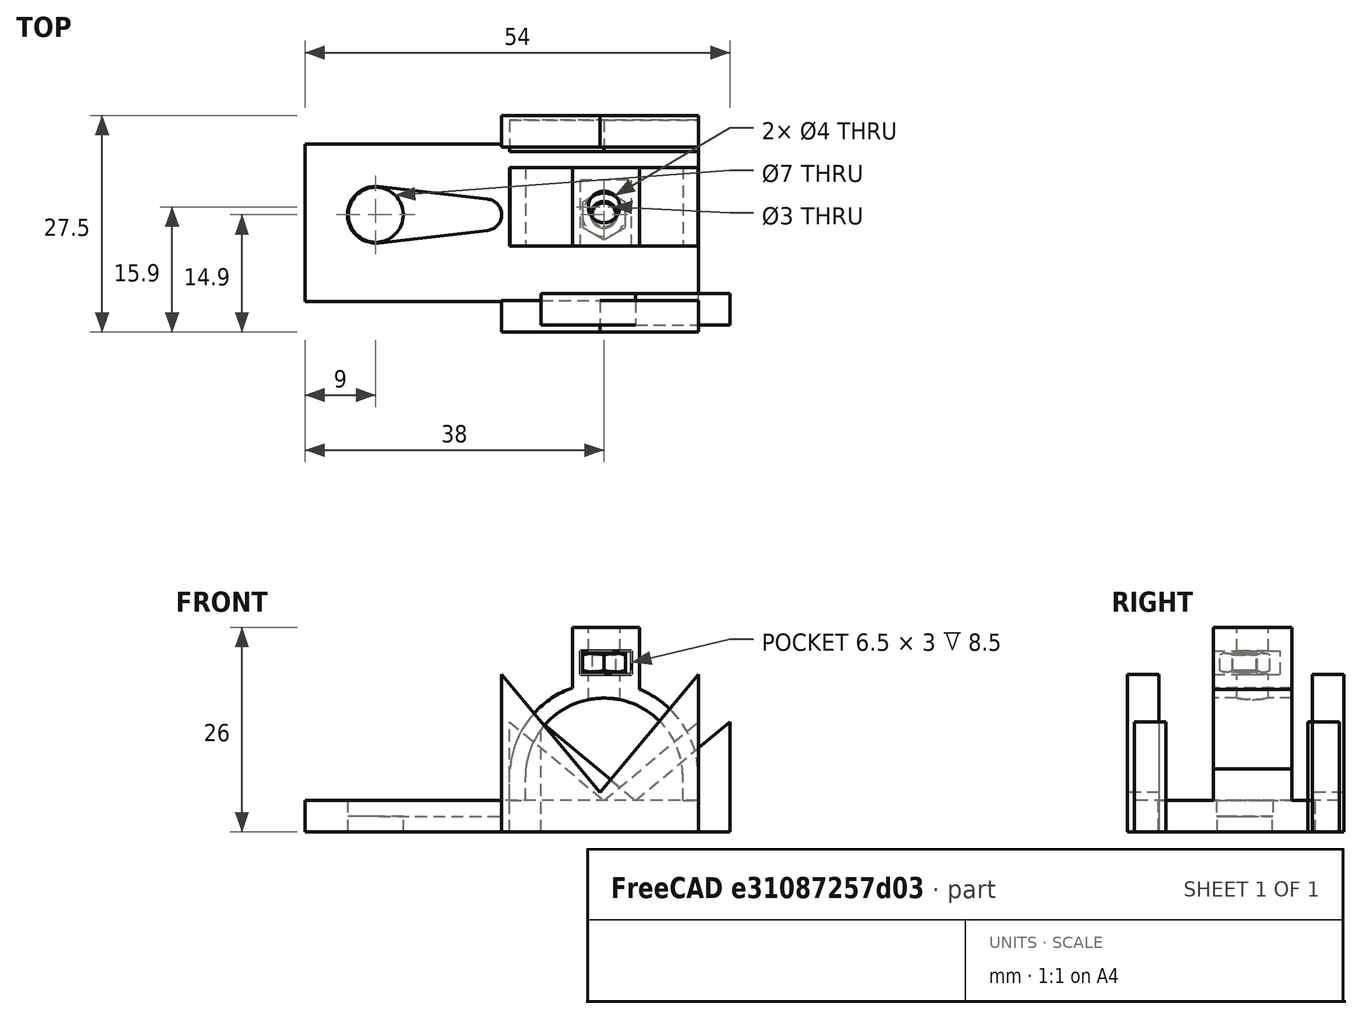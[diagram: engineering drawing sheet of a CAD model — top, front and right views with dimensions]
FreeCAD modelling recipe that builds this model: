
FCSTD DOCUMENT  (FreeCAD 0.19R24291 (Git))
Label: PENHOLDERCAD
License: All rights reserved
LicenseURL: http://en.wikipedia.org/wiki/All_rights_reserved
objects: Sketcher::SketchObject×6, Part::Box×5, PartDesign::Pad×5, PartDesign::Body×5, Part::Cut×5, Part::Cylinder×4, App::Part×3, Part::Feature×3, Part::MultiFuse×2, Mesh::Feature×2
note: 40 computed .brp shape members not serialized (recipe doc carries the construction recipe); baked Part::Feature solids carry a one-line shape summary decoded from their .brp

FEATURE [Part::Box] Box  label="Cube"
  AttacherType = Attacher::AttachEngine3D
  Height = 4
  Length = 50
  Placement = pos=(0,5,-1) rot=(0,0,1;0rad)
  Width = 20
FEATURE [Sketcher::SketchObject] Sketch
  FullyConstrained = false
  MapMode = 5
  Support = -> [XY_Plane]
  sketch-geometry (5):
    g0: ArcOfCircle CenterX=0 CenterY=0 CenterZ=0 NormalX=0 NormalY=0 NormalZ=1 AngleXU=0 Radius=3.6 StartAngle=1.45626 EndAngle=4.82692
    g1: Circle CenterX=40.9326 CenterY=0 CenterZ=0 NormalX=0 NormalY=0 NormalZ=1 AngleXU=0 Radius=0
    g2: ArcOfCircle CenterX=14 CenterY=0 CenterZ=0 NormalX=0 NormalY=0 NormalZ=1 AngleXU=0 Radius=2 StartAngle=4.82692 EndAngle=7.73945
    g3: LineSegment StartX=0.411429 StartY=3.57641 StartZ=0 EndX=14.2286 EndY=1.9869 EndZ=0
    g4: LineSegment StartX=14.2286 StartY=-1.9869 StartZ=0 EndX=0.411429 EndY=-3.57641 EndZ=0
  constraints (9):
    c: Coincident(g0,g-1)
    c: Radius(g0) = 3.6
    c: PointOnObject(g2,g-1)
    c: Radius(g2) = 2
    c: DistanceX(g0,g2) = 14
    c: Tangent(g0,g3) = 1.5708
    c: Tangent(g0,g4) = 1.5708
    c: Tangent(g2,g4) = 1.5708
    c: Tangent(g2,g3) = 1.5708
FEATURE [PartDesign::Pad] Pad
  Direction = (1,1,1)
  Length = 5
  Length2 = 100
  Profile = -> Sketch
  Type = 0
FEATURE [PartDesign::Body] Body
  Group = -> [Sketch,Pad]
  Origin = -> Origin
  Placement = pos=(9,16,1) rot=(0,0,1;0rad)
  Tip = -> Pad
FEATURE [Part::Cylinder] Cylinder
  Angle = 360
  AttacherType = Attacher::AttachEngine3D
  Height = 10
  Placement = pos=(9,16,-3) rot=(0,0,1;0rad)
  Radius = 3.5
FEATURE [Part::Cut] Cut
  Base = -> Box
  Tool = -> Body
FEATURE [Part::Cut] Cut001
  Base = -> Cut
  Tool = -> Cylinder
FEATURE [Part::Cylinder] Cylinder001
  Angle = 180
  AttacherType = Attacher::AttachEngine3D
  Height = 10
  Radius = 10
FEATURE [Part::Cylinder] Cylinder002
  Angle = 180
  AttacherType = Attacher::AttachEngine3D
  Height = 10
  Radius = 12
FEATURE [Part::Cut] Cut002
  Base = -> Cylinder002
  Placement = pos=(38,22,6) rot=(1,0,0;1.5708rad)
  Tool = -> Cylinder001
FEATURE [Part::Box] Box001  label="Cube001"
  AttacherType = Attacher::AttachEngine3D
  Height = 6
  Length = 2
  Placement = pos=(48,12,1) rot=(0,0,1;0rad)
  Width = 10
FEATURE [Part::Box] Box002  label="Cube002"
  AttacherType = Attacher::AttachEngine3D
  Height = 6
  Length = 2
  Placement = pos=(26,12,1) rot=(0,0,1;0rad)
  Width = 10
FEATURE [Part::MultiFuse] Fusion
  Shapes = -> [Box002,Box001,Cut002,Cut001]
FEATURE [Sketcher::SketchObject] Sketch002
  FullyConstrained = true
  MapMode = 5
  Support = -> [XY_Plane003]
  sketch-geometry (5):
    g0: LineSegment StartX=0 StartY=0 StartZ=0 EndX=0 EndY=14 EndZ=0
    g1: LineSegment StartX=0 StartY=14 StartZ=0 EndX=12 EndY=4 EndZ=0
    g2: LineSegment StartX=12 StartY=4 StartZ=0 EndX=24 EndY=14 EndZ=0
    g3: LineSegment StartX=24 StartY=14 StartZ=0 EndX=24 EndY=0 EndZ=0
    g4: LineSegment StartX=24 StartY=0 StartZ=0 EndX=0 EndY=0 EndZ=0
  constraints (14):
    c: Coincident(g0,g1)
    c: Coincident(g1,g2)
    c: Coincident(g2,g3)
    c: Coincident(g3,g4)
    c: Coincident(g4,g0)
    c: Horizontal(g4)
    c: Vertical(g0)
    c: Vertical(g3)
    c: DistanceX(g4,g4) = 24
    c: DistanceY(g0,g0) = 14
    c: DistanceY(g3,g3) = 14
    c: DistanceY(g0,g1) = 4
    c: DistanceX(g0,g1) = 12
    c: Coincident(g0,g-1)
FEATURE [PartDesign::Pad] Pad001
  Direction = (1,1,1)
  Length = 4
  Length2 = 100
  Profile = -> Sketch002
  Type = 0
FEATURE [PartDesign::Body] Body001
  Group = -> [Sketch002,Pad001]
  Origin = -> Origin002
  Placement = pos=(30,6,-1) rot=(1,0,0;1.5708rad)
  Tip = -> Pad001
FEATURE [App::Part] Part
  Group = -> [Body001]
  Origin = -> Origin001
  Placement = pos=(-4,0,0) rot=(0,0,1;0rad)
FEATURE [Sketcher::SketchObject] Sketch003
  FullyConstrained = true
  MapMode = 5
  Support = -> [XY_Plane004]
  sketch-geometry (5):
    g0: LineSegment StartX=0 StartY=0 StartZ=0 EndX=0 EndY=14 EndZ=0
    g1: LineSegment StartX=0 StartY=14 StartZ=0 EndX=12 EndY=4 EndZ=0
    g2: LineSegment StartX=12 StartY=4 StartZ=0 EndX=24 EndY=14 EndZ=0
    g3: LineSegment StartX=24 StartY=14 StartZ=0 EndX=24 EndY=0 EndZ=0
    g4: LineSegment StartX=24 StartY=0 StartZ=0 EndX=0 EndY=0 EndZ=0
  constraints (14):
    c: Coincident(g0,g1)
    c: Coincident(g1,g2)
    c: Coincident(g2,g3)
    c: Coincident(g3,g4)
    c: Coincident(g4,g0)
    c: Horizontal(g4)
    c: Vertical(g0)
    c: Vertical(g3)
    c: DistanceX(g4,g4) = 24
    c: DistanceY(g0,g0) = 14
    c: DistanceY(g3,g3) = 14
    c: DistanceY(g0,g1) = 4
    c: DistanceX(g0,g1) = 12
    c: Coincident(g0,g-1)
FEATURE [PartDesign::Pad] Pad002
  Direction = (1,1,1)
  Length = 4
  Length2 = 100
  Profile = -> Sketch003
  Type = 0
FEATURE [PartDesign::Body] Body002
  Group = -> [Sketch003,Pad002]
  Origin = -> Origin003
  Placement = pos=(26,28,-1) rot=(1,0,0;1.5708rad)
  Tip = -> Pad002
FEATURE [Mesh::Feature] Mesh  label="Cut003 (Meshed)"
FEATURE [Sketcher::SketchObject] Sketch004
  FullyConstrained = true
  MapMode = 5
  Placement = pos=(0,0,0) rot=(1,0,0;1.5708rad)
  Support = -> [XZ_Plane005]
  sketch-geometry (5):
    g0: LineSegment StartX=25 StartY=20 StartZ=0 EndX=37.5 EndY=5 EndZ=0
    g1: LineSegment StartX=37.5 StartY=5 StartZ=0 EndX=50 EndY=20 EndZ=0
    g2: LineSegment StartX=50 StartY=20 StartZ=0 EndX=50 EndY=0 EndZ=0
    g3: LineSegment StartX=25 StartY=20 StartZ=0 EndX=25 EndY=0 EndZ=0
    g4: LineSegment StartX=25 StartY=0 StartZ=0 EndX=50 EndY=0 EndZ=0
  constraints (15):
    c: Coincident(g0,g1)
    c: Coincident(g1,g2)
    c: Vertical(g2)
    c: PointOnObject(g2,g-1)
    c: Coincident(g0,g3)
    c: Vertical(g3)
    c: Coincident(g3,g4)
    c: Horizontal(g4)
    c: Coincident(g2,g4)
    c: DistanceX(g-1,g2) = 50
    c: DistanceX(g3,g2) = 25
    c: DistanceX(g0,g0) = 12.5
    c: DistanceY(g3,g3) = 20
    c: DistanceY(g2,g2) = 20
    c: DistanceY(g0,g0) = 15
FEATURE [PartDesign::Pad] Pad003
  Direction = (1,1,1)
  Length = 4
  Length2 = 100
  Placement = pos=(0,0,0) rot=(1,0,0;1.5708rad)
  Profile = -> Sketch004
  Type = 0
FEATURE [PartDesign::Body] Body003
  Group = -> [Sketch004,Pad003]
  Origin = -> Origin005
  Placement = pos=(0,5.1,-1) rot=(0,0,1;0rad)
  Tip = -> Pad003
FEATURE [App::Part] Part001
  Group = -> [Body003]
  Origin = -> Origin004
FEATURE [Sketcher::SketchObject] Sketch005
  FullyConstrained = true
  MapMode = 5
  Placement = pos=(0,0,0) rot=(1,0,0;1.5708rad)
  Support = -> [XZ_Plane006]
  sketch-geometry (5):
    g0: LineSegment StartX=25 StartY=20 StartZ=0 EndX=37.5 EndY=5 EndZ=0
    g1: LineSegment StartX=37.5 StartY=5 StartZ=0 EndX=50 EndY=20 EndZ=0
    g2: LineSegment StartX=50 StartY=20 StartZ=0 EndX=50 EndY=0 EndZ=0
    g3: LineSegment StartX=25 StartY=20 StartZ=0 EndX=25 EndY=0 EndZ=0
    g4: LineSegment StartX=25 StartY=0 StartZ=0 EndX=50 EndY=0 EndZ=0
  constraints (15):
    c: Coincident(g0,g1)
    c: Coincident(g1,g2)
    c: Vertical(g2)
    c: PointOnObject(g2,g-1)
    c: Coincident(g0,g3)
    c: Vertical(g3)
    c: Coincident(g3,g4)
    c: Horizontal(g4)
    c: Coincident(g2,g4)
    c: DistanceX(g-1,g2) = 50
    c: DistanceX(g3,g2) = 25
    c: DistanceX(g0,g0) = 12.5
    c: DistanceY(g3,g3) = 20
    c: DistanceY(g2,g2) = 20
    c: DistanceY(g0,g0) = 15
FEATURE [Sketcher::SketchObject] Sketch006
  FullyConstrained = true
  MapMode = 5
  Placement = pos=(0,0,0) rot=(1,0,0;1.5708rad)
  Support = -> [XZ_Plane007]
  sketch-geometry (5):
    g0: LineSegment StartX=25 StartY=20 StartZ=0 EndX=37.5 EndY=5 EndZ=0
    g1: LineSegment StartX=37.5 StartY=5 StartZ=0 EndX=50 EndY=20 EndZ=0
    g2: LineSegment StartX=50 StartY=20 StartZ=0 EndX=50 EndY=0 EndZ=0
    g3: LineSegment StartX=25 StartY=20 StartZ=0 EndX=25 EndY=0 EndZ=0
    g4: LineSegment StartX=25 StartY=0 StartZ=0 EndX=50 EndY=0 EndZ=0
  constraints (15):
    c: Coincident(g0,g1)
    c: Coincident(g1,g2)
    c: Vertical(g2)
    c: PointOnObject(g2,g-1)
    c: Coincident(g0,g3)
    c: Vertical(g3)
    c: Coincident(g3,g4)
    c: Horizontal(g4)
    c: Coincident(g2,g4)
    c: DistanceX(g-1,g2) = 50
    c: DistanceX(g3,g2) = 25
    c: DistanceX(g0,g0) = 12.5
    c: DistanceY(g3,g3) = 20
    c: DistanceY(g2,g2) = 20
    c: DistanceY(g0,g0) = 15
FEATURE [PartDesign::Pad] Pad004
  Direction = (1,1,1)
  Length = 4
  Length2 = 100
  Placement = pos=(0,0,0) rot=(1,0,0;1.5708rad)
  Profile = -> Sketch006
  Type = 0
FEATURE [PartDesign::Body] Body004
  Group = -> [Sketch006,Pad004]
  Origin = -> Origin007
  Placement = pos=(0,5.1,-1) rot=(0,0,1;0rad)
  Tip = -> Pad004
FEATURE [App::Part] Part002
  Group = -> [Body004]
  Origin = -> Origin006
  Placement = pos=(0,23.5,0) rot=(0,0,1;0rad)
FEATURE [Part::Feature] Part001_solid  label="Part001 (Solid)"
  shape: bbox 25 x 4 x 20 mm, 7 faces (baked)
FEATURE [Part::Feature] Part002_solid  label="Part002 (Solid)"
  shape: bbox 25 x 4 x 20 mm, 7 faces (baked)
FEATURE [Part::Feature] Chamfer_solid  label="Chamfer (Solid)"
  Placement = pos=(38,16,19.3) rot=(0,0,1;0rad)
  shape: bbox 6.35 x 6.35 x 2.4 mm, 29 faces (baked)
FEATURE [Part::Box] Box003  label="Cube003"
  AttacherType = Attacher::AttachEngine3D
  Height = 8
  Length = 8.5
  Placement = pos=(34,12,17) rot=(0,0,1;0rad)
  Width = 10
FEATURE [Part::Cylinder] Cylinder005  label="Cilindro"
  Angle = 360
  AttacherType = Attacher::AttachEngine3D
  Height = 10
  Placement = pos=(38,17,15) rot=(0,0,1;0rad)
  Radius = 2
FEATURE [Part::Box] Box004  label="Cubo"
  AttacherType = Attacher::AttachEngine3D
  Height = 3
  Length = 6.5
  Placement = pos=(35,12,19) rot=(0,0,1;0rad)
  Width = 8.5
FEATURE [Part::Cut] Cut003
  Base = -> Box003
  Tool = -> Box004
FEATURE [Part::MultiFuse] Fusion001
  Shapes = -> [Cut003,Fusion,Part001,Part002]
FEATURE [Part::Cut] Cut004
  Base = -> Fusion001
  Tool = -> Cylinder005
FEATURE [Mesh::Feature] ISO4762_Hex_Socket_Head_Cap_Screw_M3x16
  Placement = pos=(38,17,29) rot=(0,0,1;0rad)
